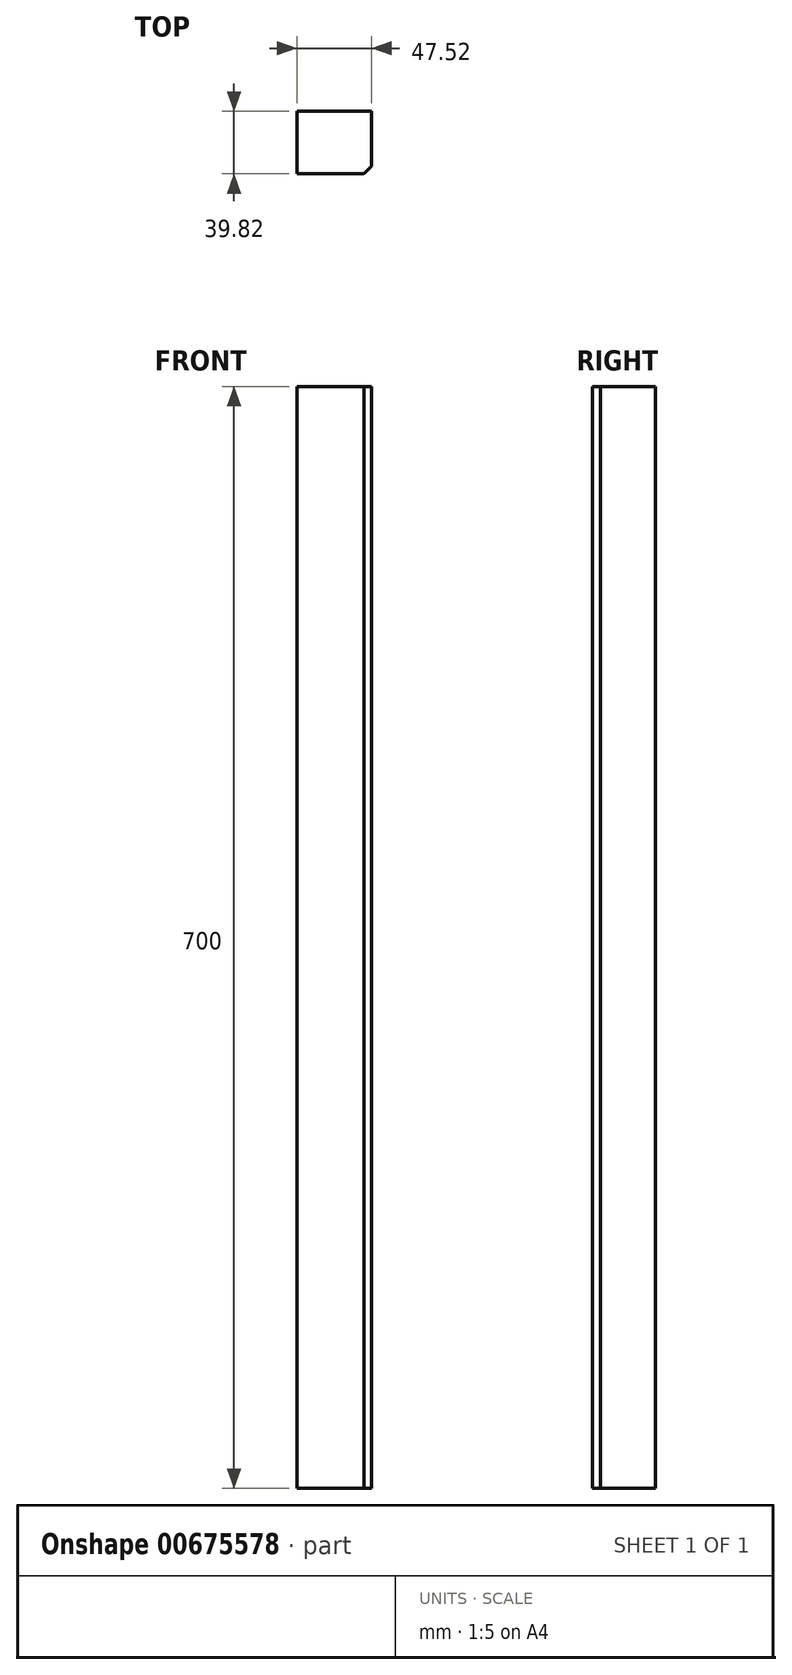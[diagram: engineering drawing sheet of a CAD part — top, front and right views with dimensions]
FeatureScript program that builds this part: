
annotation { "Feature Type Name" : "Feature", "Feature Type Description" : "" }
export const myFeature = defineFeature(function(context is Context, id is Id, definition is map)
    precondition{}
    {
        {
            var Q0;
            Q0=qCreatedBy(makeId("Top.planeOp"),FACE);
            var sketch = newSketch(context, id + "F0", { "sketchPlane" : qUnion([Q0])});
            skLineSegment(sketch, "E0.bottom", {"start": v(-47.52, 39.82) * mm, "end": v(0, 39.82) * mm});
            skLineSegment(sketch, "E0.top", {"start": v(-47.52, 0) * mm, "end": v(0, 0) * mm});
            skLineSegment(sketch, "E0.left", {"start": v(-47.52, 39.82) * mm, "end": v(-47.52, 0) * mm});
            skLineSegment(sketch, "E0.right", {"start": v(0, 39.82) * mm, "end": v(0, 0) * mm});
            skSolve(sketch);
        }
        {
            var Q0;
            Q0 = qSketchRegion(id + "F0", true);
            extrude(context, id + "F1", {"entities" : qUnion([Q0]), "depth" : 700 * mm, "offsetDistance" : 25 * mm});
        }
        {
            var Q0;
            Q0=makeQuery(id+"F1.opExtrude","SWEPT_EDGE",EDGE,{"disambiguationData":[OSD([sQuery(id+"F0.wireOp",EDGE,"E0.top"),sQuery(id+"F0.wireOp",EDGE,"E0.right")])]});
            chamfer(context, id + "F2", {"entities" : qUnion([Q0]), "width" : 5 * mm, "tangentPropagation" : true});
        }
    });
